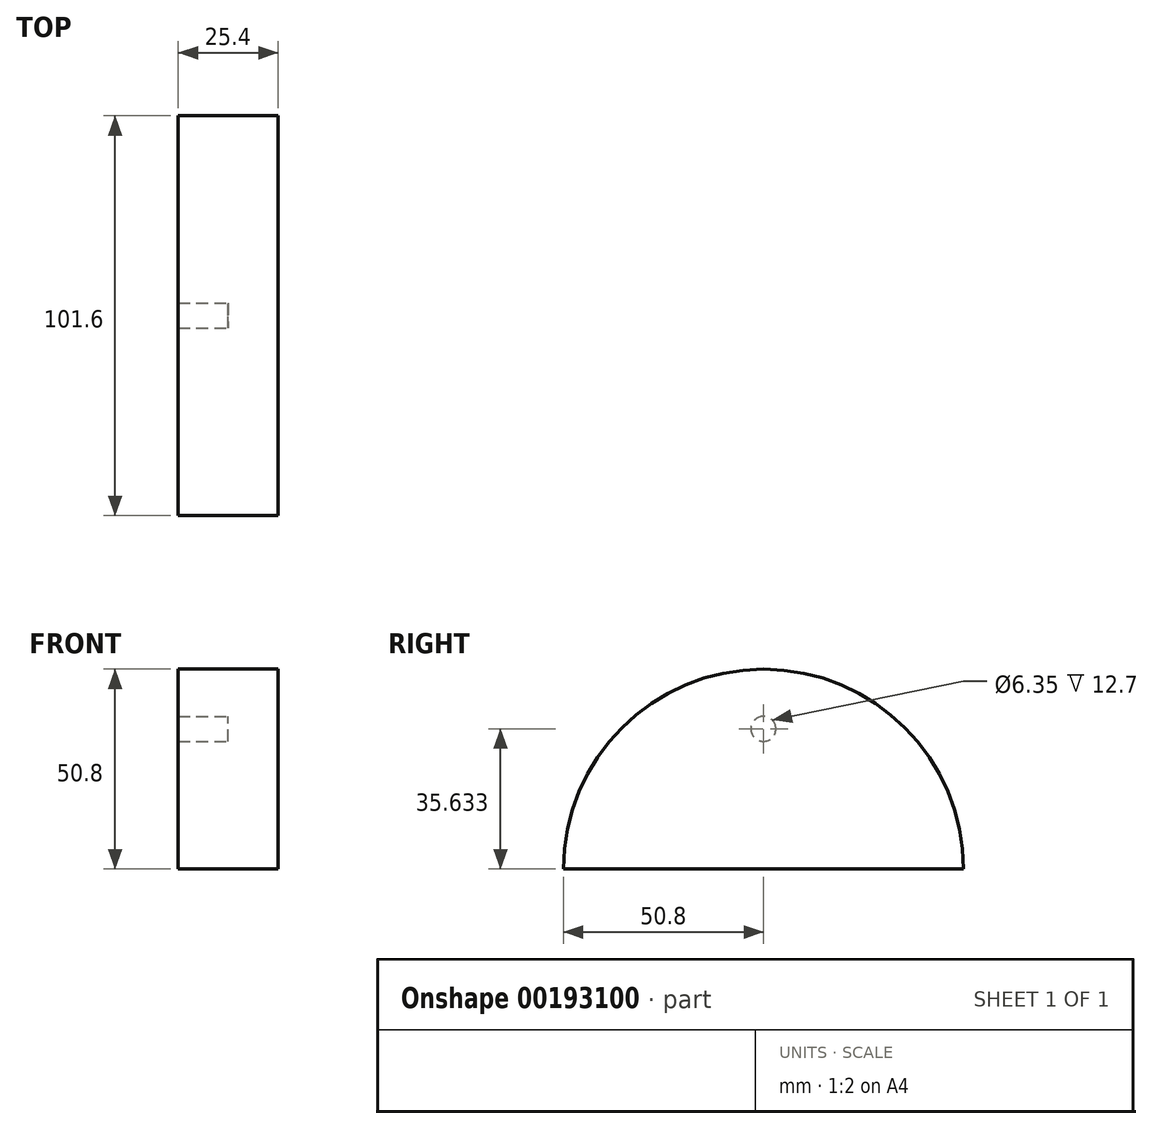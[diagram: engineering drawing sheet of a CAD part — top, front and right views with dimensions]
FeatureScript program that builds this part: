
annotation { "Feature Type Name" : "Feature", "Feature Type Description" : "" }
export const myFeature = defineFeature(function(context is Context, id is Id, definition is map)
    precondition{}
    {
        {
            var Q0;
            Q0=qCreatedBy(makeId("Top.planeOp"),FACE);
            var sketch = newSketch(context, id + "F0", { "sketchPlane" : qUnion([Q0])});
            skLineSegment(sketch, "E0.bottom", {"start": v(12.7, 0) * mm, "end": v(-12.7, 0) * mm});
            skLineSegment(sketch, "E0.top", {"start": v(12.7, -50.8) * mm, "end": v(-12.7, -50.8) * mm});
            skLineSegment(sketch, "E0.left", {"start": v(12.7, 0) * mm, "end": v(12.7, -50.8) * mm});
            skLineSegment(sketch, "E0.right", {"start": v(-12.7, 0) * mm, "end": v(-12.7, -50.8) * mm});
            skPoint(sketch, "E0.middle", {"position": v(0, -25.4) * mm});
            skSolve(sketch);
        }
        {
            var Q0;
            Q0 = qSketchRegion(id + "F0", true);
            var Q1;
            Q1=sQuery(id+"F0.wireOp",EDGE,"E0.bottom");
            revolve(context, id + "F1", {"entities" : qUnion([Q0]), "axis" : qUnion([Q1]), "revolveType" : RevolveType.ONE_DIRECTION, "angle" : 180 * degree});
        }
        {
            var Q0;
            Q0=qCreatedBy(makeId("Right.planeOp"),FACE);
            var sketch = newSketch(context, id + "F2", { "sketchPlane" : qUnion([Q0])});
            skPoint(sketch, "E1", {"position": v(0, 35.63) * mm});
            skSolve(sketch);
        }
        {
            var Q0;
            Q0=sQuery(id+"F2.wireOp",VERTEX,"E1");
            var Q1;
            Q1=makeQuery(id+"F1.opRevolve","SWEPT_BODY",BODY,{"disambiguationData":[OSD([sQuery(id+"F0.wireOp",EDGE,"E0.bottom"),sQuery(id+"F0.wireOp",EDGE,"E0.top"),sQuery(id+"F0.wireOp",EDGE,"E0.left"),sQuery(id+"F0.wireOp",EDGE,"E0.right")])]});
            hole(context, id + "F3", {"style" : HoleStyle.SIMPLE, "endStyle" : HoleEndStyle.THROUGH, "holeDiameter" : 6.35 * mm, "locations" : qUnion([Q0]), "scope" : qUnion([Q1]), "isTappedThrough" : true});
        }
    });
